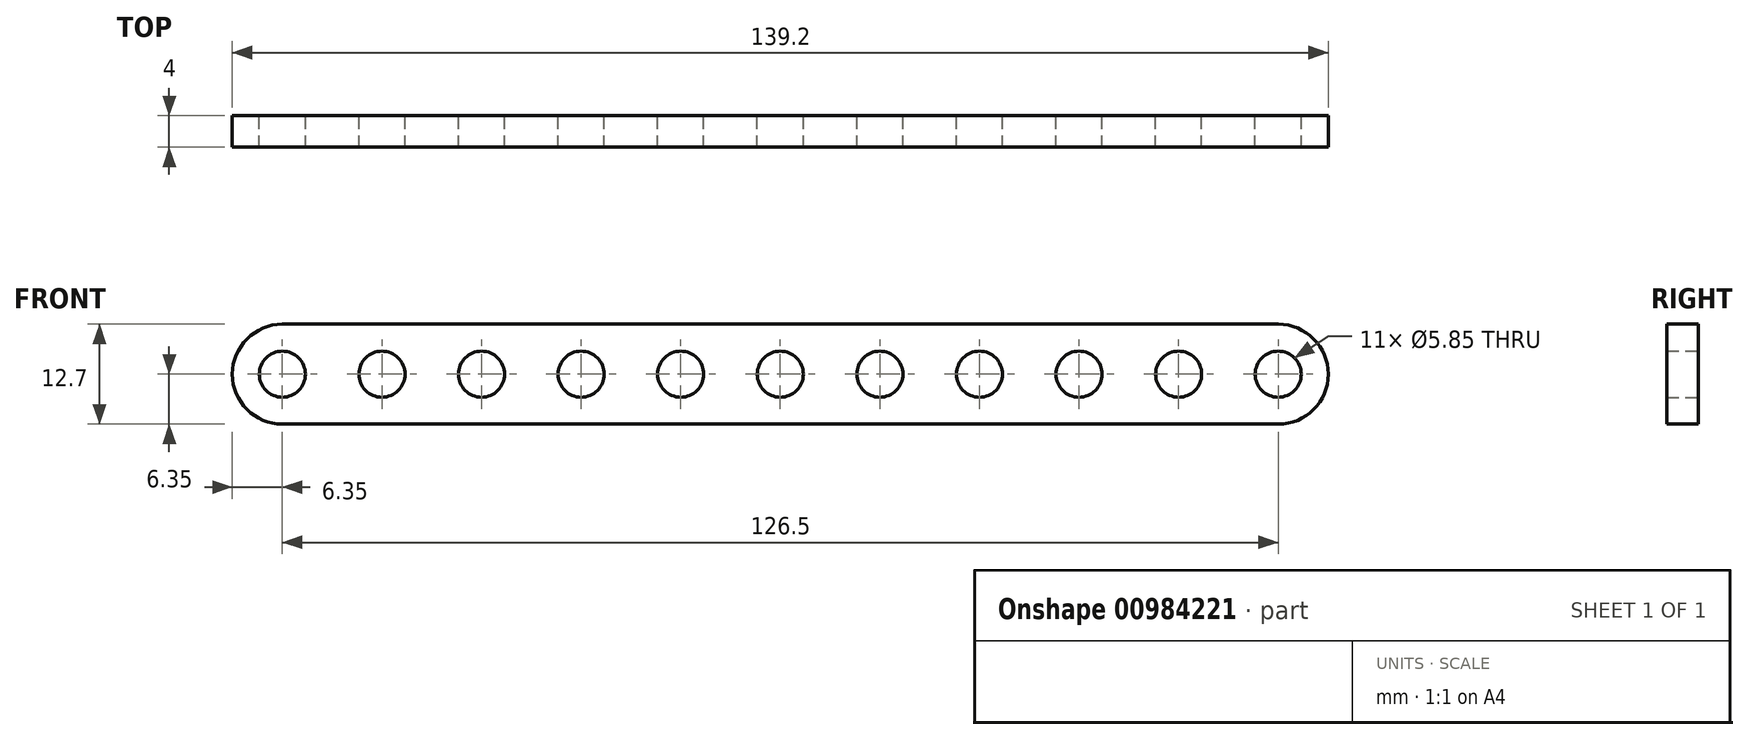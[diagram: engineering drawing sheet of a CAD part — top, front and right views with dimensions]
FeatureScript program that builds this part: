
annotation { "Feature Type Name" : "Feature", "Feature Type Description" : "" }
export const myFeature = defineFeature(function(context is Context, id is Id, definition is map)
    precondition{}
    {
        {
            var Q0;
            Q0=qCreatedBy(makeId("Front.planeOp"),FACE);
            var sketch = newSketch(context, id + "F0", { "sketchPlane" : qUnion([Q0])});
            skLineSegment(sketch, "E0.bottom", {"start": v(6.35, 0) * mm, "end": v(132.85, 0) * mm});
            skLineSegment(sketch, "E0.top", {"start": v(6.35, 12.7) * mm, "end": v(132.85, 12.7) * mm});
            skLineSegment(sketch, "E0.left", {"start": v(0, 6.35) * mm, "end": v(0, 6.35) * mm});
            skLineSegment(sketch, "E0.right", {"start": v(139.2, 6.35) * mm, "end": v(139.2, 6.35) * mm});
            skPoint(sketch, "E1.centerSnap0", {"position": v(0, 6.35) * mm});
            skPoint(sketch, "E2.visualSharp", {"position": v(0, 12.7) * mm});
            skArc(sketch, "E2.filletArc", {"start": v(6.35, 12.7) * mm, "mid": v(1.86, 10.84) * mm, "end": v(0, 6.35) * mm});
            skPoint(sketch, "E3.visualSharp", {"position": v(0, 0) * mm});
            skArc(sketch, "E3.filletArc", {"start": v(0, 6.35) * mm, "mid": v(1.86, 1.86) * mm, "end": v(6.35, 0) * mm});
            skPoint(sketch, "E4.visualSharp", {"position": v(139.2, 12.7) * mm});
            skArc(sketch, "E4.filletArc", {"start": v(139.2, 6.35) * mm, "mid": v(137.34, 10.84) * mm, "end": v(132.85, 12.7) * mm});
            skPoint(sketch, "E5.visualSharp", {"position": v(139.2, 0) * mm});
            skArc(sketch, "E5.filletArc", {"start": v(132.85, 0) * mm, "mid": v(137.34, 1.86) * mm, "end": v(139.2, 6.35) * mm});
            skCircle(sketch, "E6", {"center": v(6.35, 6.35) * mm, "radius": 2.93 * mm});
            skCircle(sketch, "E7.1.0.0", {"center": v(19, 6.35) * mm, "radius": 2.93 * mm});
            skCircle(sketch, "E7.2.0.0", {"center": v(31.65, 6.35) * mm, "radius": 2.93 * mm});
            skCircle(sketch, "E7.3.0.0", {"center": v(44.3, 6.35) * mm, "radius": 2.93 * mm});
            skCircle(sketch, "E7.4.0.0", {"center": v(56.95, 6.35) * mm, "radius": 2.93 * mm});
            skCircle(sketch, "E7.5.0.0", {"center": v(69.6, 6.35) * mm, "radius": 2.93 * mm});
            skCircle(sketch, "E7.6.0.0", {"center": v(82.25, 6.35) * mm, "radius": 2.93 * mm});
            skCircle(sketch, "E7.7.0.0", {"center": v(94.9, 6.35) * mm, "radius": 2.93 * mm});
            skCircle(sketch, "E7.8.0.0", {"center": v(107.55, 6.35) * mm, "radius": 2.93 * mm});
            skCircle(sketch, "E7.9.0.0", {"center": v(120.2, 6.35) * mm, "radius": 2.93 * mm});
            skCircle(sketch, "E7.10.0.0", {"center": v(132.85, 6.35) * mm, "radius": 2.93 * mm});
            skLineSegment(sketch, "E7.direction1", {"start": v(6.35, 6.35) * mm, "end": v(19, 6.35) * mm, "construction": true});
            skSolve(sketch);
        }
        {
            var Q0;
            Q0 = qSketchRegion(id + "F0", true);
            extrude(context, id + "F1", {"entities" : qUnion([Q0]), "depth" : 4 * mm, "offsetDistance" : 25.4 * mm});
        }
    });
